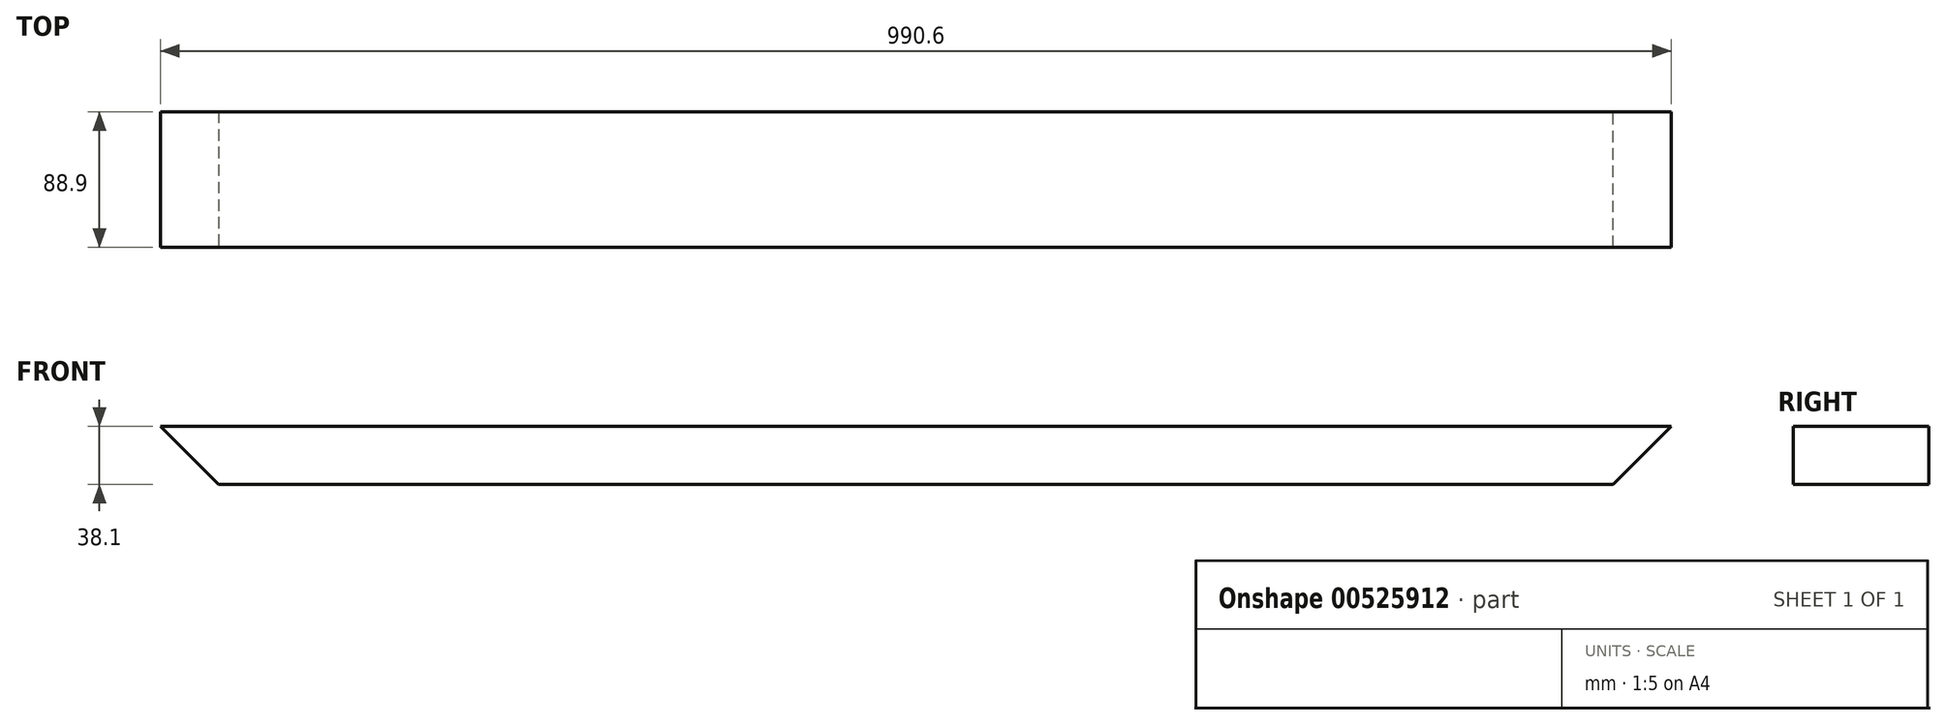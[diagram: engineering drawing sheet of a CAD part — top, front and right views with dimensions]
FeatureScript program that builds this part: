
annotation { "Feature Type Name" : "Feature", "Feature Type Description" : "" }
export const myFeature = defineFeature(function(context is Context, id is Id, definition is map)
    precondition{}
    {
        {
            var Q0;
            Q0=qCreatedBy(makeId("Front.planeOp"),FACE);
            var sketch = newSketch(context, id + "F0", { "sketchPlane" : qUnion([Q0])});
            skLineSegment(sketch, "E0.bottom", {"start": v(-495.3, -19.05) * mm, "end": v(495.3, -19.05) * mm});
            skLineSegment(sketch, "E0.top", {"start": v(-495.3, 19.05) * mm, "end": v(495.3, 19.05) * mm});
            skLineSegment(sketch, "E0.left", {"start": v(-495.3, -19.05) * mm, "end": v(-495.3, 19.05) * mm});
            skLineSegment(sketch, "E0.right", {"start": v(495.3, -19.05) * mm, "end": v(495.3, 19.05) * mm});
            skPoint(sketch, "E0.middle", {"position": v(0, 0) * mm});
            skSolve(sketch);
        }
        {
            var Q0;
            Q0 = qSketchRegion(id + "F0", true);
            extrude(context, id + "F1", {"entities" : qUnion([Q0]), "depth" : 88.9 * mm, "offsetDistance" : 25.4 * mm});
        }
        {
            var Q0;
            Q0=makeQuery(id+"F1.opExtrude","CAP_FACE",FACE,{"disambiguationData":[OSD([sQuery(id+"F0.wireOp",EDGE,"E0.bottom"),sQuery(id+"F0.wireOp",EDGE,"E0.top"),sQuery(id+"F0.wireOp",EDGE,"E0.left"),sQuery(id+"F0.wireOp",EDGE,"E0.right")])],"isStart":false});
            var sketch = newSketch(context, id + "F2", { "sketchPlane" : qUnion([Q0])});
            skLineSegment(sketch, "E1", {"start": v(-495.3, 19.05) * mm, "end": v(-457.2, -19.05) * mm});
            skLineSegment(sketch, "E2", {"start": v(-457.2, -19.05) * mm, "end": v(-495.3, -19.05) * mm});
            skLineSegment(sketch, "E3", {"start": v(-495.3, -19.05) * mm, "end": v(-495.3, 19.05) * mm});
            skSolve(sketch);
        }
        {
            var Q0;
            Q0 = qSketchRegion(id + "F2", true);
            extrude(context, id + "F3", {"entities" : qUnion([Q0]), "operationType" : NewBodyOperationType.REMOVE, "endBound" : BoundingType.THROUGH_ALL, "oppositeDirection" : true, "depth" : 25.4 * mm, "offsetDistance" : 25.4 * mm});
        }
        {
            var Q0;
            Q0=qCreatedBy(makeId("Front.planeOp"),FACE);
            var sketch = newSketch(context, id + "F4", { "sketchPlane" : qUnion([Q0])});
            skLineSegment(sketch, "E4", {"start": v(495.3, 19.05) * mm, "end": v(457.2, -19.05) * mm});
            skLineSegment(sketch, "E5", {"start": v(457.2, -19.05) * mm, "end": v(495.3, -19.05) * mm});
            skLineSegment(sketch, "E6", {"start": v(495.3, -19.05) * mm, "end": v(495.3, 19.05) * mm});
            skSolve(sketch);
        }
        {
            var Q0;
            Q0 = qSketchRegion(id + "F4", true);
            extrude(context, id + "F5", {"entities" : qUnion([Q0]), "operationType" : NewBodyOperationType.REMOVE, "endBound" : BoundingType.THROUGH_ALL, "depth" : 25.4 * mm, "offsetDistance" : 25.4 * mm});
        }
    });
